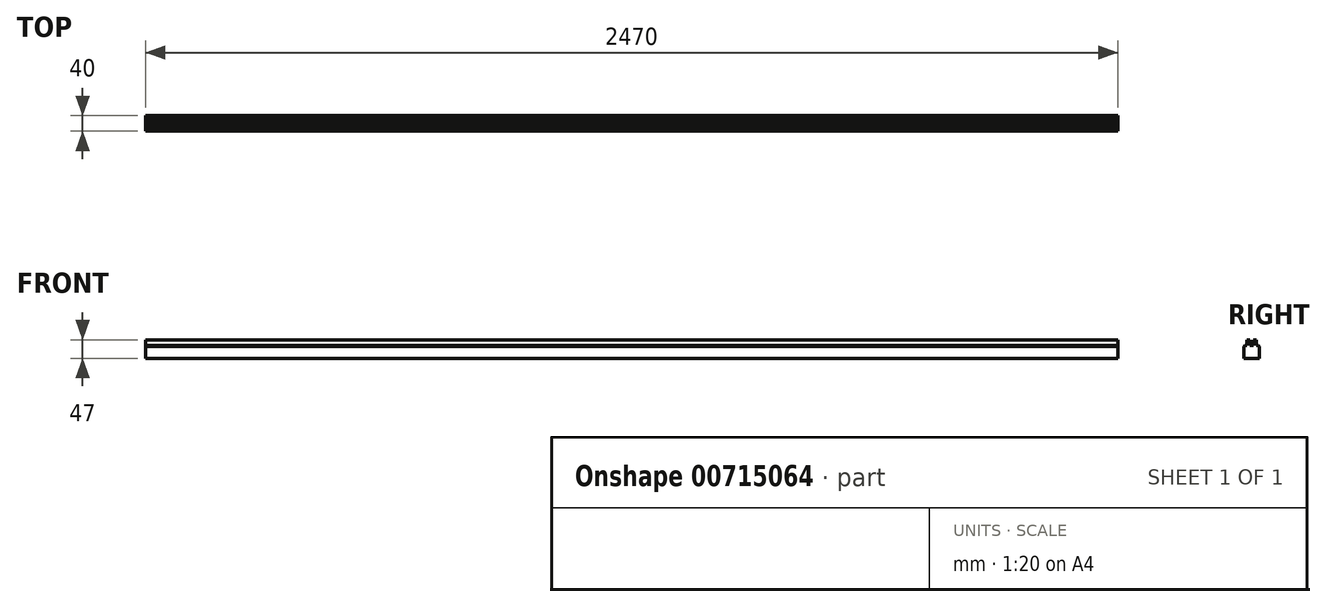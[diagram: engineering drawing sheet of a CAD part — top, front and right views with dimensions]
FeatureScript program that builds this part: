
annotation { "Feature Type Name" : "Feature", "Feature Type Description" : "" }
export const myFeature = defineFeature(function(context is Context, id is Id, definition is map)
    precondition{}
    {
        {
            assignVariable(context, id + "F0", {"name" : "Laenge", "anyValue" : 2550});
        }
        {
            var Q0;
            Q0=qCreatedBy(makeId("Right.planeOp"),FACE);
            var sketch = newSketch(context, id + "F1", { "sketchPlane" : qUnion([Q0])});
            skLineSegment(sketch, "E0", {"start": v(20, 63) * mm, "end": v(20, -63) * mm});
            skLineSegment(sketch, "E1", {"start": v(20, -63) * mm, "end": v(17, -66) * mm});
            skLineSegment(sketch, "E2", {"start": v(17, -66) * mm, "end": v(12, -66) * mm});
            skLineSegment(sketch, "E3", {"start": v(12, -52) * mm, "end": v(12, -66) * mm});
            skLineSegment(sketch, "E4", {"start": v(12, -52) * mm, "end": v(4, -52) * mm});
            skLineSegment(sketch, "E5", {"start": v(4, -66) * mm, "end": v(4, -52) * mm});
            skLineSegment(sketch, "E6", {"start": v(4, -66) * mm, "end": v(-4, -66) * mm});
            skLineSegment(sketch, "E7", {"start": v(-4, -52) * mm, "end": v(-4, -66) * mm});
            skLineSegment(sketch, "E8", {"start": v(-4, -52) * mm, "end": v(-12, -52) * mm});
            skLineSegment(sketch, "E9", {"start": v(-12, -66) * mm, "end": v(-12, -52) * mm});
            skLineSegment(sketch, "E10", {"start": v(-12, -66) * mm, "end": v(-17, -66) * mm});
            skLineSegment(sketch, "E11", {"start": v(-17, -66) * mm, "end": v(-20, -63) * mm});
            skLineSegment(sketch, "E12", {"start": v(-20, -63) * mm, "end": v(-20, 63) * mm});
            skLineSegment(sketch, "E13", {"start": v(-20, 63) * mm, "end": v(-17, 66) * mm});
            skLineSegment(sketch, "E14", {"start": v(-17, 66) * mm, "end": v(-12, 66) * mm});
            skLineSegment(sketch, "E15", {"start": v(-4, 66) * mm, "end": v(4, 66) * mm});
            skLineSegment(sketch, "E16", {"start": v(12, 66) * mm, "end": v(17, 66) * mm});
            skLineSegment(sketch, "E17", {"start": v(17, 66) * mm, "end": v(20, 63) * mm});
            skPoint(sketch, "E18.end.orphan", {"position": v(12, 57.8) * mm});
            skPoint(sketch, "E19.end.orphan", {"position": v(4, 66.3) * mm});
            skPoint(sketch, "E20.end.orphan", {"position": v(-4, 66.3) * mm});
            skLineSegment(sketch, "E21", {"start": v(-12, 66) * mm, "end": v(-12, 80) * mm});
            skLineSegment(sketch, "E22", {"start": v(-12, 80) * mm, "end": v(-4, 80) * mm});
            skLineSegment(sketch, "E23", {"start": v(-4, 80) * mm, "end": v(-4, 66) * mm});
            skLineSegment(sketch, "E24", {"start": v(4, 66) * mm, "end": v(4, 80) * mm});
            skLineSegment(sketch, "E25", {"start": v(4, 80) * mm, "end": v(12, 80) * mm});
            skLineSegment(sketch, "E26", {"start": v(12, 80) * mm, "end": v(12, 66) * mm});
            skLineSegment(sketch, "E27", {"start": v(20, -33) * mm, "end": v(-20, -33) * mm});
            skLineSegment(sketch, "E28", {"start": v(20, 33) * mm, "end": v(-20, 33) * mm});
            skPoint(sketch, "E29.end.orphan", {"position": v(-141.42, 0) * mm});
            skLineSegment(sketch, "E30", {"start": v(20, 0) * mm, "end": v(-20, 0) * mm});
            skLineSegment(sketch, "E31", {"start": v(20, 0) * mm, "end": v(-20, 0) * mm, "construction": true});
            skLineSegment(sketch, "E32", {"start": v(0, 33) * mm, "end": v(0, -33) * mm, "construction": true});
            skLineSegment(sketch, "E33", {"start": v(20, 14) * mm, "end": v(-20, 14) * mm});
            skSolve(sketch);
        }
        {
            var Q0;
            Q0=qCreatedBy(makeId("Front.planeOp"),FACE);
            var sketch = newSketch(context, id + "F2", { "sketchPlane" : qUnion([Q0])});
            skLineSegment(sketch, "E34", {"start": v(1275, 0) * mm, "end": v(-1275, 0) * mm, "construction": true});
            skPoint(sketch, "E35.right.start.orphan", {"position": v(-259.12, 108.1) * mm});
            skPoint(sketch, "E36.left.start.orphan", {"position": v(237.35, 108.1) * mm});
            skPoint(sketch, "E37.left.end.orphan", {"position": v(237.35, -84.05) * mm});
            skPoint(sketch, "E37.bottom.start.orphan", {"position": v(237.35, -117.05) * mm});
            skPoint(sketch, "E38.right.start.orphan", {"position": v(-259.12, -117.05) * mm});
            skPoint(sketch, "E38.top.end.orphan", {"position": v(-259.12, -84.05) * mm});
            skLineSegment(sketch, "E39.bottom", {"start": v(-1315, 33) * mm, "end": v(-1235, 33) * mm});
            skLineSegment(sketch, "E39.top", {"start": v(-1315, 133) * mm, "end": v(-1235, 133) * mm});
            skLineSegment(sketch, "E39.left", {"start": v(-1315, 33) * mm, "end": v(-1315, 133) * mm});
            skLineSegment(sketch, "E39.right", {"start": v(-1235, 33) * mm, "end": v(-1235, 133) * mm});
            skPoint(sketch, "E39.middle", {"position": v(-1275, 83) * mm});
            skLineSegment(sketch, "E40.bottom", {"start": v(-1315, -133) * mm, "end": v(-1235, -133) * mm});
            skLineSegment(sketch, "E40.top", {"start": v(-1315, -33) * mm, "end": v(-1235, -33) * mm});
            skLineSegment(sketch, "E40.left", {"start": v(-1315, -133) * mm, "end": v(-1315, -33) * mm});
            skLineSegment(sketch, "E40.right", {"start": v(-1235, -133) * mm, "end": v(-1235, -33) * mm});
            skPoint(sketch, "E40.middle", {"position": v(-1275, -83) * mm});
            skLineSegment(sketch, "E41.bottom", {"start": v(1315, 33) * mm, "end": v(1235, 33) * mm});
            skLineSegment(sketch, "E41.top", {"start": v(1315, 133) * mm, "end": v(1235, 133) * mm});
            skLineSegment(sketch, "E41.left", {"start": v(1315, 33) * mm, "end": v(1315, 133) * mm});
            skLineSegment(sketch, "E41.right", {"start": v(1235, 33) * mm, "end": v(1235, 133) * mm});
            skPoint(sketch, "E41.middle", {"position": v(1275, 83) * mm});
            skLineSegment(sketch, "E42.bottom", {"start": v(1315, -33) * mm, "end": v(1235, -33) * mm});
            skLineSegment(sketch, "E42.top", {"start": v(1315, -133) * mm, "end": v(1235, -133) * mm});
            skLineSegment(sketch, "E42.left", {"start": v(1315, -33) * mm, "end": v(1315, -133) * mm});
            skLineSegment(sketch, "E42.right", {"start": v(1235, -33) * mm, "end": v(1235, -133) * mm});
            skPoint(sketch, "E42.middle", {"position": v(1275, -83) * mm});
            skSolve(sketch);
        }
        {
            var Q0;
            {var subQ3=sQuery(id+"F1.wireOp",EDGE,"E13");Q0=makeQuery(id+"F1.imprint","IMPRINT",FACE,{"disambiguationData":[TD([[makeQuery(id+"F1.imprint","IMPRINT",EDGE,{"derivedFrom":subQ3}),-1.0]])]});}
            var Q1;
            {var subQ0=sQuery(id+"F1.wireOp",EDGE,"E28");Q1=makeQuery(id+"F1.imprint","IMPRINT",FACE,{"disambiguationData":[TD([[makeQuery(id+"F1.imprint","IMPRINT",EDGE,{"derivedFrom":subQ0}),1.0]])]});}
            extrude(context, id + "F3", {"entities" : qUnion([Q0, Q1]), "endBound" : BoundingType.SYMMETRIC, "depth" : getVariable(context, 'Laenge') * mm, "offsetDistance" : 25 * mm});
        }
        {
            var Q0;
            Q0=makeQuery(id+"F2.imprint","IMPRINT",FACE,{"disambiguationData":[TD([[makeQuery(id+"F2.imprint","IMPRINT",EDGE,{"derivedFrom":sQuery(id+"F2.wireOp",EDGE,"E39.bottom")}),1.0]])]});
            var Q1;
            Q1=makeQuery(id+"F2.imprint","IMPRINT",FACE,{"disambiguationData":[TD([[makeQuery(id+"F2.imprint","IMPRINT",EDGE,{"derivedFrom":sQuery(id+"F2.wireOp",EDGE,"E40.bottom")}),1.0]])]});
            var Q2;
            Q2=makeQuery(id+"F2.imprint","IMPRINT",FACE,{"disambiguationData":[TD([[makeQuery(id+"F2.imprint","IMPRINT",EDGE,{"derivedFrom":sQuery(id+"F2.wireOp",EDGE,"E41.bottom")}),-1.0]])]});
            var Q3;
            Q3=makeQuery(id+"F2.imprint","IMPRINT",FACE,{"disambiguationData":[TD([[makeQuery(id+"F2.imprint","IMPRINT",EDGE,{"derivedFrom":sQuery(id+"F2.wireOp",EDGE,"E42.bottom")}),1.0]])]});
            extrude(context, id + "F4", {"entities" : qUnion([Q0, Q1, Q2, Q3]), "operationType" : NewBodyOperationType.REMOVE, "endBound" : BoundingType.SYMMETRIC, "oppositeDirection" : true, "depth" : 50 * mm, "offsetDistance" : 25 * mm});
        }
        {
            var Q0;
            Q0=makeQuery(id+"F3.opExtrude","SWEPT_FACE",FACE,{"disambiguationData":[OSD([sQuery(id+"F1.wireOp",EDGE,"E12")])]});
            var sketch = newSketch(context, id + "F5", { "sketchPlane" : qUnion([Q0])});
            skLineSegment(sketch, "E43.bottom", {"start": v(-1275, 33) * mm, "end": v(1275, 33) * mm});
            skLineSegment(sketch, "E43.top", {"start": v(-1275, 14) * mm, "end": v(1275, 14) * mm});
            skLineSegment(sketch, "E43.left", {"start": v(-1275, 33) * mm, "end": v(-1275, 14) * mm});
            skLineSegment(sketch, "E43.right", {"start": v(1275, 33) * mm, "end": v(1275, 14) * mm});
            skSolve(sketch);
        }
        {
            var Q0;
            Q0=makeQuery(id+"F5.imprint","IMPRINT",FACE,{"disambiguationData":[TD([[makeQuery(id+"F5.imprint","IMPRINT",EDGE,{"derivedFrom":sQuery(id+"F5.wireOp",EDGE,"E43.top")}),-1.0]])]});
            extrude(context, id + "F6", {"entities" : qUnion([Q0]), "operationType" : NewBodyOperationType.REMOVE, "endBound" : BoundingType.UP_TO_NEXT, "oppositeDirection" : true, "depth" : 25 * mm, "offsetDistance" : 25 * mm});
        }
    });
